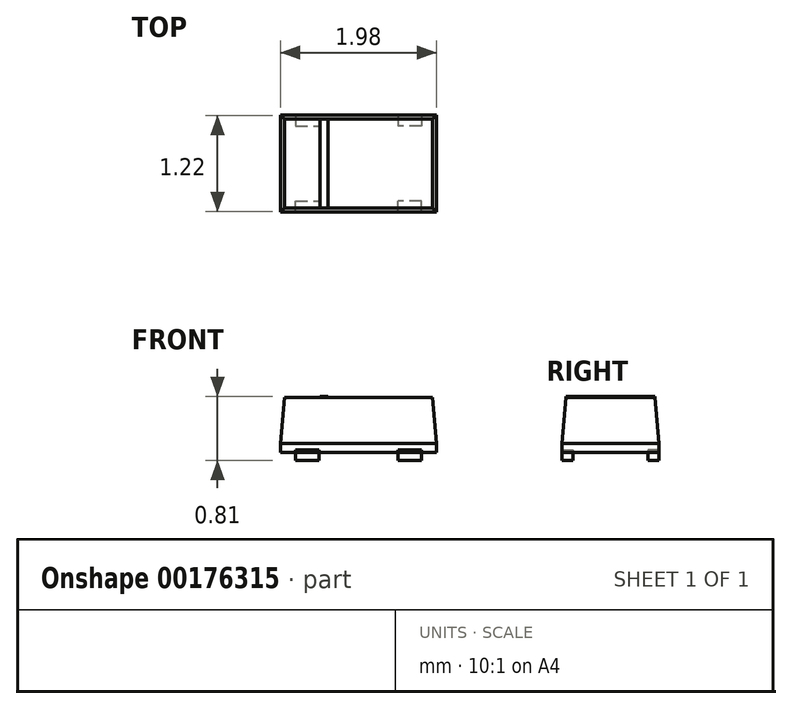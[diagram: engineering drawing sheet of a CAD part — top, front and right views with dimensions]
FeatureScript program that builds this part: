
annotation { "Feature Type Name" : "Feature", "Feature Type Description" : "" }
export const myFeature = defineFeature(function(context is Context, id is Id, definition is map)
    precondition{}
    {
        {
            var Q0;
            Q0=qCreatedBy(makeId("Top.planeOp"),FACE);
            var sketch = newSketch(context, id + "F0", { "sketchPlane" : qUnion([Q0])});
            skLineSegment(sketch, "E0.bottom", {"start": v(0.8, -1.05) * mm, "end": v(-0.8, -1.05) * mm, "construction": true});
            skLineSegment(sketch, "E0.top", {"start": v(0.8, 1.05) * mm, "end": v(-0.8, 1.05) * mm, "construction": true});
            skLineSegment(sketch, "E0.left", {"start": v(0.8, -1.05) * mm, "end": v(0.8, 1.05) * mm, "construction": true});
            skLineSegment(sketch, "E0.right", {"start": v(-0.8, -1.05) * mm, "end": v(-0.8, 1.05) * mm, "construction": true});
            skPoint(sketch, "E0.middle", {"position": v(0, 0) * mm});
            skLineSegment(sketch, "E1.bottom", {"start": v(-0.8, 1.05) * mm, "end": v(-0.5, 1.05) * mm});
            skLineSegment(sketch, "E1.top", {"start": v(-0.8, 0.47) * mm, "end": v(-0.5, 0.47) * mm});
            skLineSegment(sketch, "E1.left", {"start": v(-0.8, 1.05) * mm, "end": v(-0.8, 0.47) * mm});
            skLineSegment(sketch, "E1.right", {"start": v(-0.5, 1.05) * mm, "end": v(-0.5, 0.47) * mm});
            skLineSegment(sketch, "E2.bottom", {"start": v(0.8, 1.05) * mm, "end": v(0.5, 1.05) * mm});
            skLineSegment(sketch, "E2.top", {"start": v(0.8, 0.48) * mm, "end": v(0.5, 0.48) * mm});
            skLineSegment(sketch, "E2.left", {"start": v(0.8, 1.05) * mm, "end": v(0.8, 0.48) * mm});
            skLineSegment(sketch, "E2.right", {"start": v(0.5, 1.05) * mm, "end": v(0.5, 0.48) * mm});
            skLineSegment(sketch, "E3.bottom", {"start": v(-0.8, -1.05) * mm, "end": v(-0.5, -1.05) * mm});
            skLineSegment(sketch, "E3.top", {"start": v(-0.8, -0.48) * mm, "end": v(-0.5, -0.48) * mm});
            skLineSegment(sketch, "E3.left", {"start": v(-0.8, -1.05) * mm, "end": v(-0.8, -0.48) * mm});
            skLineSegment(sketch, "E3.right", {"start": v(-0.5, -1.05) * mm, "end": v(-0.5, -0.48) * mm});
            skLineSegment(sketch, "E4.bottom", {"start": v(0.8, -1.05) * mm, "end": v(0.5, -1.05) * mm});
            skLineSegment(sketch, "E4.top", {"start": v(0.8, -0.47) * mm, "end": v(0.5, -0.47) * mm});
            skLineSegment(sketch, "E4.left", {"start": v(0.8, -1.05) * mm, "end": v(0.8, -0.47) * mm});
            skLineSegment(sketch, "E4.right", {"start": v(0.5, -1.05) * mm, "end": v(0.5, -0.47) * mm});
            skSolve(sketch);
        }
        {
            var Q0;
            Q0 = qSketchRegion(id + "F0", true);
            extrude(context, id + "F1", {"entities" : qUnion([Q0]), "depth" : 0.13 * mm});
        }
        {
            var Q0;
            Q0=qCreatedBy(makeId("Top.planeOp"),FACE);
            cPlane(context, id + "F2", {"entities" : qUnion([Q0]), "cplaneType" : CPlaneType.OFFSET, "offset" : 0.1 * mm, "width" : 150 * mm, "height" : 150 * mm});
        }
        {
            var Q0;
            Q0=qCreatedBy(id+"F2.planeOp",FACE);
            var sketch = newSketch(context, id + "F3", { "sketchPlane" : qUnion([Q0])});
            skLineSegment(sketch, "E5.bottom", {"start": v(1, 0.62) * mm, "end": v(-1, 0.62) * mm});
            skLineSegment(sketch, "E5.top", {"start": v(1, -0.63) * mm, "end": v(-1, -0.63) * mm});
            skLineSegment(sketch, "E5.left", {"start": v(1, 0.62) * mm, "end": v(1, -0.63) * mm});
            skLineSegment(sketch, "E5.right", {"start": v(-1, 0.62) * mm, "end": v(-1, -0.63) * mm});
            skPoint(sketch, "E5.middle", {"position": v(0, 0) * mm});
            skSolve(sketch);
        }
        {
            var Q0;
            Q0 = qSketchRegion(id + "F3", true);
            extrude(context, id + "F4", {"entities" : qUnion([Q0]), "depth" : 0.7 * mm, "hasDraft" : true, "draftAngle" : 5 * degree, "draftPullDirection" : true});
        }
        {
            var Q0;
            Q0=qCreatedBy(makeId("Top.planeOp"),FACE);
            var sketch = newSketch(context, id + "F5", { "sketchPlane" : qUnion([Q0])});
            skLineSegment(sketch, "E6.bottom", {"start": v(1, 0.61) * mm, "end": v(-1, 0.61) * mm});
            skLineSegment(sketch, "E6.top", {"start": v(1, -0.61) * mm, "end": v(-1, -0.61) * mm});
            skLineSegment(sketch, "E6.left", {"start": v(1, 0.61) * mm, "end": v(1, -0.61) * mm});
            skLineSegment(sketch, "E6.right", {"start": v(-1, 0.61) * mm, "end": v(-1, -0.61) * mm});
            skPoint(sketch, "E6.middle", {"position": v(0, 0) * mm});
            skSolve(sketch);
        }
        {
            var Q0;
            Q0 = qSketchRegion(id + "F5", true);
            extrude(context, id + "F6", {"entities" : qUnion([Q0]), "operationType" : NewBodyOperationType.INTERSECT, "endBound" : BoundingType.THROUGH_ALL, "depth" : 25 * mm});
        }
        {
            var Q0;
            Q0=makeQuery(id+"F4.opExtrude","CAP_FACE",FACE,{"disambiguationData":[OSD([sQuery(id+"F3.wireOp",EDGE,"E5.bottom"),sQuery(id+"F3.wireOp",EDGE,"E5.top"),sQuery(id+"F3.wireOp",EDGE,"E5.left"),sQuery(id+"F3.wireOp",EDGE,"E5.right")])],"isStart":false});
            var sketch = newSketch(context, id + "F7", { "sketchPlane" : qUnion([Q0])});
            skLineSegment(sketch, "E7.bottom", {"start": v(-0.5, 0.56) * mm, "end": v(-0.4, 0.56) * mm});
            skLineSegment(sketch, "E7.top", {"start": v(-0.5, -0.56) * mm, "end": v(-0.4, -0.56) * mm});
            skLineSegment(sketch, "E7.left", {"start": v(-0.5, 0.56) * mm, "end": v(-0.5, -0.56) * mm});
            skLineSegment(sketch, "E7.right", {"start": v(-0.4, 0.56) * mm, "end": v(-0.4, -0.56) * mm});
            skSolve(sketch);
        }
        {
            var Q0;
            Q0=makeQuery(id+"F7.imprint","IMPRINT",FACE,{"disambiguationData":[TD([[makeQuery(id+"F7.imprint","IMPRINT",EDGE,{"derivedFrom":sQuery(id+"F7.wireOp",EDGE,"E7.bottom")}),1.0]])]});
            extrude(context, id + "F8", {"entities" : qUnion([Q0]), "depth" : 0.01 * mm});
        }
    });
